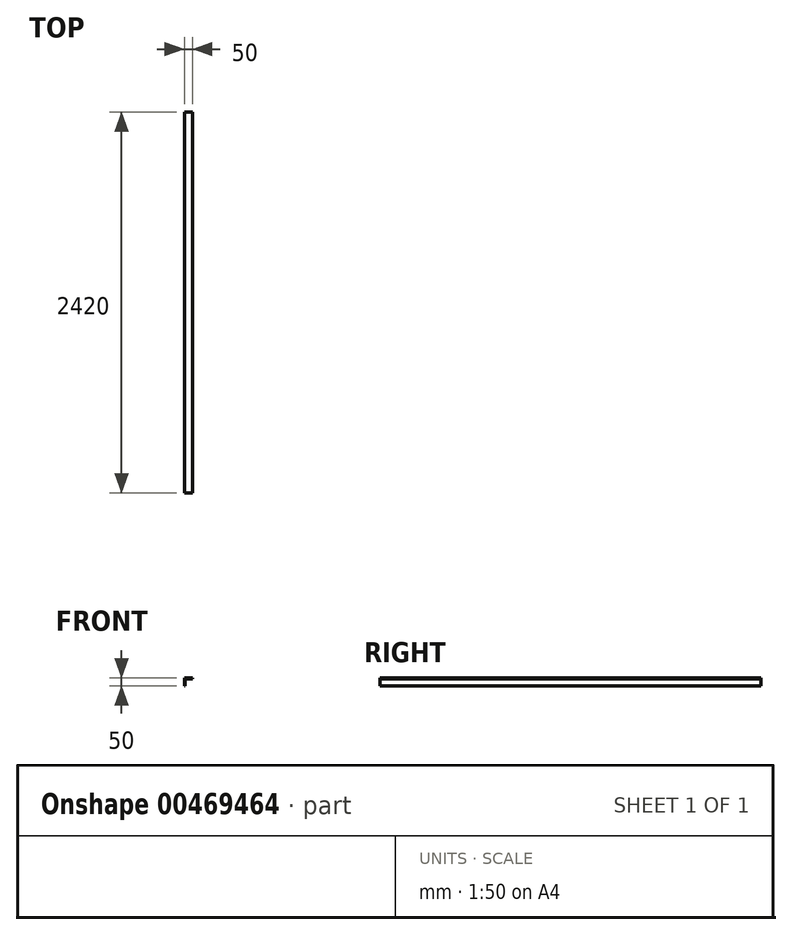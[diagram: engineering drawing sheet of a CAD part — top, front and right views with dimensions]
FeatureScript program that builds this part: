
annotation { "Feature Type Name" : "Feature", "Feature Type Description" : "" }
export const myFeature = defineFeature(function(context is Context, id is Id, definition is map)
    precondition{}
    {
        {
            var Q0;
            Q0=qCreatedBy(makeId("Front.planeOp"),FACE);
            var sketch = newSketch(context, id + "F0", { "sketchPlane" : qUnion([Q0])});
            skLineSegment(sketch, "E0", {"start": v(0, 0) * mm, "end": v(0, 50) * mm});
            skLineSegment(sketch, "E1", {"start": v(0, 50) * mm, "end": v(50, 50) * mm});
            skLineSegment(sketch, "E2", {"start": v(50, 50) * mm, "end": v(50, 45) * mm});
            skLineSegment(sketch, "E3", {"start": v(50, 45) * mm, "end": v(5, 45) * mm});
            skLineSegment(sketch, "E4", {"start": v(5, 45) * mm, "end": v(5, 0) * mm});
            skLineSegment(sketch, "E5", {"start": v(5, 0) * mm, "end": v(0, 0) * mm});
            skSolve(sketch);
        }
        {
            var Q0;
            Q0 = qSketchRegion(id + "F0", true);
            extrude(context, id + "F1", {"entities" : qUnion([Q0]), "depth" : 2420 * mm});
        }
    });
